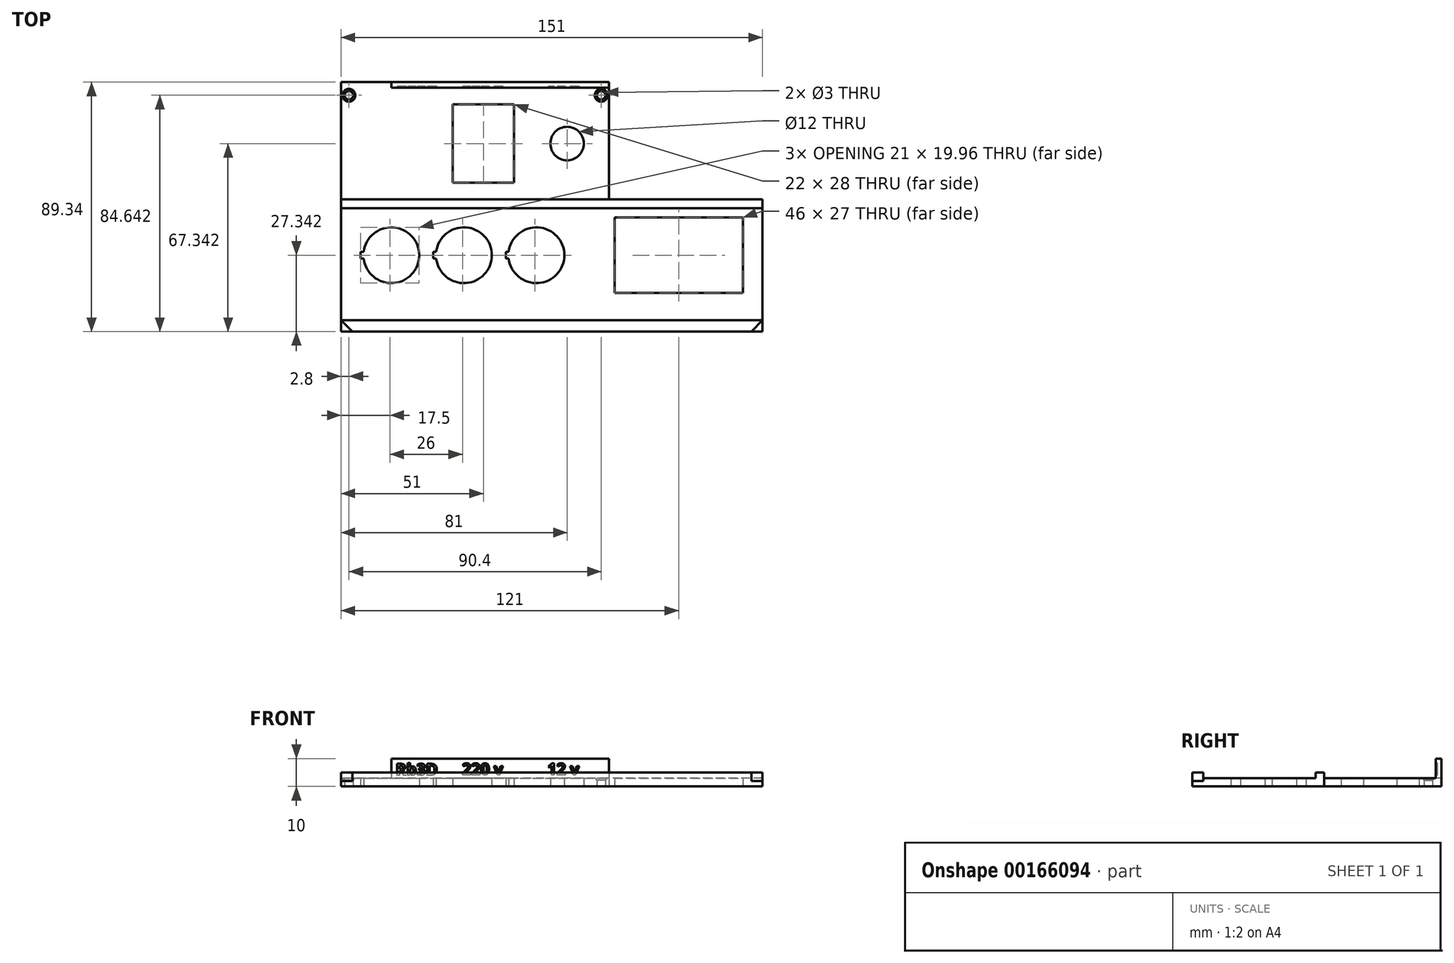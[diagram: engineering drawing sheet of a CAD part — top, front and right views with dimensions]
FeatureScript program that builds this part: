
annotation { "Feature Type Name" : "Feature", "Feature Type Description" : "" }
export const myFeature = defineFeature(function(context is Context, id is Id, definition is map)
    precondition{}
    {
        {
            var Q0;
            Q0=qCreatedBy(makeId("Top.planeOp"),FACE);
            var sketch = newSketch(context, id + "F0", { "sketchPlane" : qUnion([Q0])});
            skLineSegment(sketch, "E0.0", {"start": v(151, 0) * mm, "end": v(0, 0) * mm});
            skLineSegment(sketch, "E0.1", {"start": v(96, 89.34) * mm, "end": v(48, 89.34) * mm});
            skLineSegment(sketch, "E0.2", {"start": v(96, 89.34) * mm, "end": v(96, 47.34) * mm});
            skLineSegment(sketch, "E0.3", {"start": v(0, 0) * mm, "end": v(0, 89.34) * mm});
            skLineSegment(sketch, "E0.4", {"start": v(96, 47.34) * mm, "end": v(151, 47.34) * mm});
            skLineSegment(sketch, "E0.5", {"start": v(151, 0) * mm, "end": v(151, 47.34) * mm});
            skLineSegment(sketch, "E1", {"start": v(151, 27.34) * mm, "end": v(0, 27.34) * mm, "construction": true});
            skLineSegment(sketch, "E2", {"start": v(18, 46.21) * mm, "end": v(18, -10) * mm, "construction": true});
            skArc(sketch, "E3", {"start": v(8.08, 26.1) * mm, "mid": v(28, 27.34) * mm, "end": v(8.08, 28.6) * mm});
            skArc(sketch, "E4", {"start": v(34.08, 26.1) * mm, "mid": v(54, 27.34) * mm, "end": v(34.08, 28.6) * mm});
            skArc(sketch, "E5", {"start": v(60.08, 26.1) * mm, "mid": v(80, 27.34) * mm, "end": v(60.08, 28.6) * mm});
            skLineSegment(sketch, "E6", {"start": v(48, 89.34) * mm, "end": v(0, 89.34) * mm});
            skLineSegment(sketch, "E7", {"start": v(125.77, 67.34) * mm, "end": v(5.34, 67.34) * mm, "construction": true});
            skLineSegment(sketch, "E8.bottom", {"start": v(62, 53.34) * mm, "end": v(40, 53.34) * mm});
            skLineSegment(sketch, "E8.top", {"start": v(62, 81.34) * mm, "end": v(40, 81.34) * mm});
            skLineSegment(sketch, "E8.left", {"start": v(62, 53.34) * mm, "end": v(62, 81.34) * mm});
            skLineSegment(sketch, "E8.right", {"start": v(40, 53.34) * mm, "end": v(40, 81.34) * mm});
            skPoint(sketch, "E8.middle", {"position": v(51, 67.34) * mm});
            skCircle(sketch, "E9", {"center": v(81, 67.34) * mm, "radius": 6 * mm});
            skLineSegment(sketch, "E10", {"start": v(18, 87.34) * mm, "end": v(96, 87.34) * mm});
            skCircle(sketch, "E11", {"center": v(18, 27.34) * mm, "radius": 11.5 * mm, "construction": true});
            skCircle(sketch, "E12", {"center": v(44, 27.34) * mm, "radius": 11.5 * mm, "construction": true});
            skCircle(sketch, "E13", {"center": v(70, 27.34) * mm, "radius": 11.5 * mm, "construction": true});
            skLineSegment(sketch, "E14.bottom", {"start": v(63.5, 82.84) * mm, "end": v(38.5, 82.84) * mm, "construction": true});
            skLineSegment(sketch, "E14.top", {"start": v(63.5, 51.84) * mm, "end": v(38.5, 51.84) * mm, "construction": true});
            skLineSegment(sketch, "E14.left", {"start": v(63.5, 82.84) * mm, "end": v(63.5, 51.84) * mm, "construction": true});
            skLineSegment(sketch, "E14.right", {"start": v(38.5, 82.84) * mm, "end": v(38.5, 51.84) * mm, "construction": true});
            skLineSegment(sketch, "E15", {"start": v(18, 89.34) * mm, "end": v(18, 87.34) * mm});
            skLineSegment(sketch, "E16", {"start": v(0, 84.64) * mm, "end": v(96, 84.64) * mm, "construction": true});
            skCircle(sketch, "E17", {"center": v(2.8, 84.64) * mm, "radius": 1.5 * mm});
            skCircle(sketch, "E18", {"center": v(93.2, 84.64) * mm, "radius": 1.5 * mm});
            skLineSegment(sketch, "E19.bottom", {"start": v(98, 13.84) * mm, "end": v(144, 13.84) * mm});
            skLineSegment(sketch, "E19.top", {"start": v(98, 40.84) * mm, "end": v(144, 40.84) * mm});
            skLineSegment(sketch, "E19.left", {"start": v(98, 13.84) * mm, "end": v(98, 40.84) * mm});
            skLineSegment(sketch, "E19.right", {"start": v(144, 13.84) * mm, "end": v(144, 40.84) * mm});
            skPoint(sketch, "E19.middle", {"position": v(121, 27.34) * mm});
            skLineSegment(sketch, "E20.bottom", {"start": v(8.08, 26.1) * mm, "end": v(7, 26.1) * mm});
            skLineSegment(sketch, "E20.top", {"start": v(8.08, 28.6) * mm, "end": v(7, 28.6) * mm});
            skLineSegment(sketch, "E20.right", {"start": v(7, 26.1) * mm, "end": v(7, 28.6) * mm});
            skPoint(sketch, "E20.middle", {"position": v(8, 27.34) * mm});
            skLineSegment(sketch, "E21.bottom", {"start": v(34.08, 26.1) * mm, "end": v(33, 26.1) * mm});
            skLineSegment(sketch, "E21.top", {"start": v(34.08, 28.6) * mm, "end": v(33, 28.6) * mm});
            skLineSegment(sketch, "E21.right", {"start": v(33, 26.1) * mm, "end": v(33, 28.6) * mm});
            skPoint(sketch, "E21.middle", {"position": v(34, 27.34) * mm});
            skLineSegment(sketch, "E22.bottom", {"start": v(60.08, 28.6) * mm, "end": v(59, 28.6) * mm});
            skLineSegment(sketch, "E22.top", {"start": v(60.08, 26.1) * mm, "end": v(59, 26.1) * mm});
            skLineSegment(sketch, "E22.right", {"start": v(59, 28.6) * mm, "end": v(59, 26.1) * mm});
            skPoint(sketch, "E23.orphan", {"position": v(9, 28.6) * mm});
            skPoint(sketch, "E24.orphan", {"position": v(9, 26.1) * mm});
            skPoint(sketch, "E25.orphan", {"position": v(35, 28.6) * mm});
            skPoint(sketch, "E26.orphan", {"position": v(35, 26.1) * mm});
            skSolve(sketch);
        }
        {
            var Q0;
            Q0=makeQuery(id+"F0.imprint","IMPRINT",FACE,{"disambiguationData":[TD([[makeQuery(id+"F0.imprint","IMPRINT",EDGE,{"derivedFrom":sQuery(id+"F0.wireOp",EDGE,"E0.0")}),-1.0]])]});
            extrude(context, id + "F1", {"entities" : qUnion([Q0]), "depth" : 2 * mm});
        }
        {
            var Q0;
            {var subQ4=sQuery(id+"F0.wireOp",EDGE,"E0.1");Q0=makeQuery(id+"F0.imprint","IMPRINT",FACE,{"disambiguationData":[TD([[makeQuery(id+"F0.imprint","IMPRINT",EDGE,{"derivedFrom":subQ4}),1.0]])]});}
            extrude(context, id + "F2", {"entities" : qUnion([Q0]), "operationType" : NewBodyOperationType.ADD, "depth" : 10 * mm});
        }
        {
            var Q0;
            Q0=makeQuery(id+"F2.opExtrude","SWEPT_FACE",FACE,{"disambiguationData":[OSD([sQuery(id+"F0.wireOp",EDGE,"E10")])]});
            var sketch = newSketch(context, id + "F3", { "sketchPlane" : qUnion([Q0])});
            skText(sketch, "E27", { "text": "Rb3D", "fontName": "OpenSans-Bold.ttf"});
            skText(sketch, "E28", { "text": "220 v", "fontName": "OpenSans-Bold.ttf"});
            skText(sketch, "E29", { "text": "12 v", "fontName": "OpenSans-Bold.ttf"});
            const initialGuessF3  = {"E27": [0.01959, 0.004, 1, 0, 0.00417], "E28": [0.04332, 0.00414, 1, 0, 0.00417], "E29": [0.0739, 0.00414, 1, 0, 0.00417]};
            skSetInitialGuess(sketch, initialGuessF3);
            skSolve(sketch);
        }
        {
            var Q0;
            Q0 = qSketchRegion(id + "F3", true);
            extrude(context, id + "F4", {"entities" : qUnion([Q0]), "operationType" : NewBodyOperationType.REMOVE, "oppositeDirection" : true, "depth" : 0.5 * mm});
        }
        {
            var Q0;
            Q0=makeQuery(id+"F1.opExtrude","CAP_FACE",FACE,{"disambiguationData":[OSD([sQuery(id+"F0.wireOp",EDGE,"E0.0"),sQuery(id+"F0.wireOp",EDGE,"E0.2"),sQuery(id+"F0.wireOp",EDGE,"E0.3"),sQuery(id+"F0.wireOp",EDGE,"E0.4"),sQuery(id+"F0.wireOp",EDGE,"E0.5"),sQuery(id+"F0.wireOp",EDGE,"E3"),sQuery(id+"F0.wireOp",EDGE,"E4"),sQuery(id+"F0.wireOp",EDGE,"E5"),sQuery(id+"F0.wireOp",EDGE,"E6"),sQuery(id+"F0.wireOp",EDGE,"E8.bottom"),sQuery(id+"F0.wireOp",EDGE,"E8.top"),sQuery(id+"F0.wireOp",EDGE,"E8.left"),sQuery(id+"F0.wireOp",EDGE,"E8.right"),sQuery(id+"F0.wireOp",EDGE,"E9"),sQuery(id+"F0.wireOp",EDGE,"E10"),sQuery(id+"F0.wireOp",EDGE,"E15"),sQuery(id+"F0.wireOp",EDGE,"E17"),sQuery(id+"F0.wireOp",EDGE,"E18"),sQuery(id+"F0.wireOp",EDGE,"E19.bottom"),sQuery(id+"F0.wireOp",EDGE,"E19.top"),sQuery(id+"F0.wireOp",EDGE,"E19.left"),sQuery(id+"F0.wireOp",EDGE,"E19.right"),sQuery(id+"F0.wireOp",EDGE,"E20.bottom"),sQuery(id+"F0.wireOp",EDGE,"E20.top"),sQuery(id+"F0.wireOp",EDGE,"E20.right"),sQuery(id+"F0.wireOp",EDGE,"E21.bottom"),sQuery(id+"F0.wireOp",EDGE,"E21.top"),sQuery(id+"F0.wireOp",EDGE,"E21.right"),sQuery(id+"F0.wireOp",EDGE,"E22.bottom"),sQuery(id+"F0.wireOp",EDGE,"E22.top"),sQuery(id+"F0.wireOp",EDGE,"E22.right")])],"isStart":false});
            var sketch = newSketch(context, id + "F5", { "sketchPlane" : qUnion([Q0])});
            skLineSegment(sketch, "E30", {"start": v(0, 4) * mm, "end": v(4, 0) * mm});
            skLineSegment(sketch, "E31", {"start": v(147, 0) * mm, "end": v(151, 4) * mm});
            skSolve(sketch);
        }
        {
            var Q0;
            {var subQ34=sQuery(id+"F5.wireOp",EDGE,"E30");Q0=makeQuery(id+"F5.imprint","IMPRINT",FACE,{"disambiguationData":[TD([[makeQuery(id+"F5.imprint","IMPRINT",EDGE,{"derivedFrom":subQ34}),1.0]])]});}
            extrude(context, id + "F6", {"entities" : qUnion([Q0]), "operationType" : NewBodyOperationType.ADD, "depth" : 1 * mm});
        }
        {
            var Q0;
            Q0=makeQuery(id+"F6.opExtrude","CAP_EDGE",EDGE,{"disambiguationData":[OSD([sQuery(id+"F0.wireOp",EDGE,"E18")])],"isStart":false});
            var Q1;
            Q1=makeQuery(id+"F6.opExtrude","CAP_EDGE",EDGE,{"disambiguationData":[OSD([sQuery(id+"F0.wireOp",EDGE,"E17")])],"isStart":false});
            chamfer(context, id + "F7", {"entities" : qUnion([Q0, Q1]), "width" : .8 * mm, "tangentPropagation" : true});
        }
        {
            var Q0;
            Q0=makeQuery(id+"F6.opExtrude","CAP_FACE",FACE,{"disambiguationData":[OSD([sQuery(id+"F0.wireOp",EDGE,"E0.0"),sQuery(id+"F0.wireOp",EDGE,"E0.2"),sQuery(id+"F0.wireOp",EDGE,"E0.3"),sQuery(id+"F0.wireOp",EDGE,"E0.4"),sQuery(id+"F0.wireOp",EDGE,"E0.5"),sQuery(id+"F0.wireOp",EDGE,"E3"),sQuery(id+"F0.wireOp",EDGE,"E4"),sQuery(id+"F0.wireOp",EDGE,"E5"),sQuery(id+"F0.wireOp",EDGE,"E6"),sQuery(id+"F0.wireOp",EDGE,"E8.bottom"),sQuery(id+"F0.wireOp",EDGE,"E8.top"),sQuery(id+"F0.wireOp",EDGE,"E8.left"),sQuery(id+"F0.wireOp",EDGE,"E8.right"),sQuery(id+"F0.wireOp",EDGE,"E9"),sQuery(id+"F0.wireOp",EDGE,"E10"),sQuery(id+"F0.wireOp",EDGE,"E15"),sQuery(id+"F0.wireOp",EDGE,"E17"),sQuery(id+"F0.wireOp",EDGE,"E18"),sQuery(id+"F0.wireOp",EDGE,"E19.bottom"),sQuery(id+"F0.wireOp",EDGE,"E19.top"),sQuery(id+"F0.wireOp",EDGE,"E19.left"),sQuery(id+"F0.wireOp",EDGE,"E19.right"),sQuery(id+"F0.wireOp",EDGE,"E20.bottom"),sQuery(id+"F0.wireOp",EDGE,"E20.top"),sQuery(id+"F0.wireOp",EDGE,"E20.right"),sQuery(id+"F0.wireOp",EDGE,"E21.bottom"),sQuery(id+"F0.wireOp",EDGE,"E21.top"),sQuery(id+"F0.wireOp",EDGE,"E21.right"),sQuery(id+"F0.wireOp",EDGE,"E22.bottom"),sQuery(id+"F0.wireOp",EDGE,"E22.top"),sQuery(id+"F0.wireOp",EDGE,"E22.right"),sQuery(id+"F5.wireOp",EDGE,"E30"),sQuery(id+"F5.wireOp",EDGE,"E31")])],"isStart":false});
            var sketch = newSketch(context, id + "F8", { "sketchPlane" : qUnion([Q0])});
            skLineSegment(sketch, "E32", {"start": v(4, 0) * mm, "end": v(0, 4) * mm});
            skLineSegment(sketch, "E33", {"start": v(0, 4) * mm, "end": v(151, 4) * mm});
            skLineSegment(sketch, "E34", {"start": v(151, 4) * mm, "end": v(147, 0) * mm});
            skLineSegment(sketch, "E35", {"start": v(147, 0) * mm, "end": v(4, 0) * mm});
            skLineSegment(sketch, "E36.bottom", {"start": v(151, 47.34) * mm, "end": v(0, 47.34) * mm});
            skLineSegment(sketch, "E36.top", {"start": v(151, 44.25) * mm, "end": v(0, 44.25) * mm});
            skLineSegment(sketch, "E36.left", {"start": v(151, 47.34) * mm, "end": v(151, 44.25) * mm});
            skLineSegment(sketch, "E36.right", {"start": v(0, 47.34) * mm, "end": v(0, 44.25) * mm});
            skSolve(sketch);
        }
        {
            var Q0;
            Q0=makeQuery(id+"F8.imprint","IMPRINT",FACE,{"disambiguationData":[TD([[makeQuery(id+"F8.imprint","IMPRINT",EDGE,{"derivedFrom":sQuery(id+"F8.wireOp",EDGE,"E36.top")}),-1.0]])]});
            var Q1;
            Q1=makeQuery(id+"F8.imprint","IMPRINT",FACE,{"disambiguationData":[TD([[makeQuery(id+"F8.imprint","IMPRINT",EDGE,{"derivedFrom":sQuery(id+"F8.wireOp",EDGE,"E32")}),1.0]])]});
            extrude(context, id + "F9", {"entities" : qUnion([Q0, Q1]), "operationType" : NewBodyOperationType.ADD, "depth" : 2 * mm});
        }
    });
